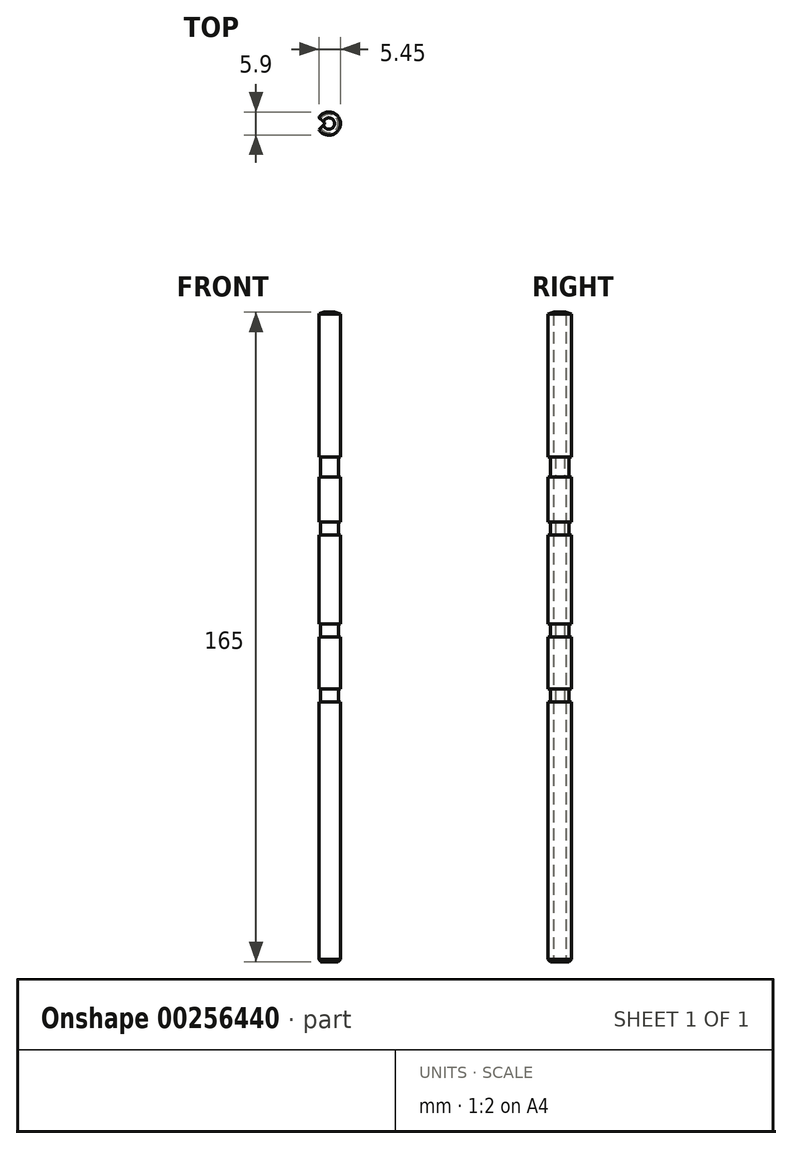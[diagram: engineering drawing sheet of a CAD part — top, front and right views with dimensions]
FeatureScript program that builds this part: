
annotation { "Feature Type Name" : "Feature", "Feature Type Description" : "" }
export const myFeature = defineFeature(function(context is Context, id is Id, definition is map)
    precondition{}
    {
        {
            var Q0;
            Q0=qCreatedBy(makeId("Top.planeOp"),FACE);
            var sketch = newSketch(context, id + "F0", { "sketchPlane" : qUnion([Q0])});
            skArc(sketch, "E0", {"start": v(-0.83, -0.52) * mm, "mid": v(0.98, 0) * mm, "end": v(-0.83, 0.52) * mm});
            skLineSegment(sketch, "E1", {"start": v(0.98, 0) * mm, "end": v(-0.32, 0) * mm, "construction": true});
            skLineSegment(sketch, "E2", {"start": v(-0.39, 0.07) * mm, "end": v(-0.83, 0.52) * mm});
            skLineSegment(sketch, "E3", {"start": v(-0.39, -0.07) * mm, "end": v(-0.83, -0.52) * mm});
            skPoint(sketch, "E4.visualSharp", {"position": v(-0.32, 0) * mm});
            skArc(sketch, "E4.filletArc", {"start": v(-0.39, -0.07) * mm, "mid": v(-0.36, 0) * mm, "end": v(-0.39, 0.07) * mm});
            skSolve(sketch);
        }
        {
            var Q0;
            Q0=makeQuery(id+"F0.imprint","IMPRINT",FACE,{"disambiguationData":[TD([[makeQuery(id+"F0.imprint","IMPRINT",EDGE,{"derivedFrom":sQuery(id+"F0.wireOp",EDGE,"E0")}),1.0]])]});
            extrude(context, id + "F1", {"entities" : qUnion([Q0]), "depth" : 55 * mm});
        }
        {
            var Q0;
            Q0=makeQuery(id+"F1.opExtrude","CAP_EDGE",EDGE,{"disambiguationData":[OSD([sQuery(id+"F0.wireOp",EDGE,"E0")])],"isStart":true});
            chamfer(context, id + "F2", {"entities" : qUnion([Q0]), "chamferType" : ChamferType.OFFSET_ANGLE, "width" : .2 * mm, "oppositeDirection" : false, "angle" : 45 * degree, "tangentPropagation" : true});
        }
        {
            var Q0;
            Q0=makeQuery(id+"F1.opExtrude","CAP_EDGE",EDGE,{"disambiguationData":[OSD([sQuery(id+"F0.wireOp",EDGE,"E0")])],"isStart":false});
            chamfer(context, id + "F3", {"entities" : qUnion([Q0]), "chamferType" : ChamferType.OFFSET_ANGLE, "width" : 0.13 * mm, "oppositeDirection" : false, "angle" : 75 * degree, "tangentPropagation" : true});
        }
        {
            var Q0;
            Q0=makeQuery(id+"F1.opExtrude","SWEPT_BODY",BODY,{"disambiguationData":[OSD([sQuery(id+"F0.wireOp",EDGE,"E0"),sQuery(id+"F0.wireOp",EDGE,"E2"),sQuery(id+"F0.wireOp",EDGE,"E3"),sQuery(id+"F0.wireOp",EDGE,"E4.filletArc")])]});
            var Q1;
            Q1=qCreatedBy(makeId("Origin.pointOp"),VERTEX);
            transform(context, id + "F4", {"entities" : qUnion([Q0]), "transformType" : TransformType.COPY});
        }
        {
            var Q0;
            Q0=makeQuery(id+"F4.opPattern","COPY",FACE,{"derivedFrom":makeQuery(id+"F1.opExtrude","CAP_FACE",FACE,{"disambiguationData":[OSD([sQuery(id+"F0.wireOp",EDGE,"E0"),sQuery(id+"F0.wireOp",EDGE,"E2"),sQuery(id+"F0.wireOp",EDGE,"E3"),sQuery(id+"F0.wireOp",EDGE,"E4.filletArc")])],"isStart":false}),"instanceName":"1"});
            cPlane(context, id + "F5", {"entities" : qUnion([Q0]), "cplaneType" : CPlaneType.OFFSET, "offset" : 18.85 * mm, "oppositeDirection" : true, "width" : 150 * mm, "height" : 150 * mm});
        }
        {
            var Q0;
            Q0=qCreatedBy(id+"F5.planeOp",FACE);
            var sketch = newSketch(context, id + "F6", { "sketchPlane" : qUnion([Q0])});
            skCircle(sketch, "E5", {"center": v(0, 0) * mm, "radius": 1.05 * mm});
            skCircle(sketch, "E6", {"center": v(0, 0) * mm, "radius": 0.8 * mm});
            skSolve(sketch);
        }
        {
            var Q0;
            Q0=makeQuery(id+"F6.imprint","IMPRINT",FACE,{"disambiguationData":[TD([[makeQuery(id+"F6.imprint","IMPRINT",EDGE,{"derivedFrom":sQuery(id+"F6.wireOp",EDGE,"E5")}),1.0]])]});
            extrude(context, id + "F7", {"entities" : qUnion([Q0]), "operationType" : NewBodyOperationType.REMOVE, "depth" : 1.1 * mm});
        }
        {
            var Q0;
            Q0=qCreatedBy(id+"F5.planeOp",FACE);
            cPlane(context, id + "F8", {"entities" : qUnion([Q0]), "cplaneType" : CPlaneType.OFFSET, "offset" : 5.5 * mm, "width" : 150 * mm, "height" : 150 * mm});
        }
        {
            var Q0;
            Q0=qCreatedBy(id+"F8.planeOp",FACE);
            var sketch = newSketch(context, id + "F9", { "sketchPlane" : qUnion([Q0])});
            skCircle(sketch, "E7", {"center": v(0, 0) * mm, "radius": 1.05 * mm});
            skCircle(sketch, "E8", {"center": v(0, 0) * mm, "radius": 0.8 * mm});
            skSolve(sketch);
        }
        {
            var Q0;
            Q0=makeQuery(id+"F9.imprint","IMPRINT",FACE,{"disambiguationData":[TD([[makeQuery(id+"F9.imprint","IMPRINT",EDGE,{"derivedFrom":sQuery(id+"F9.wireOp",EDGE,"E7")}),1.0]])]});
            extrude(context, id + "F10", {"entities" : qUnion([Q0]), "operationType" : NewBodyOperationType.REMOVE, "depth" : 1.1 * mm});
        }
        {
            var Q0;
            Q0=makeQuery(id+"F1.opExtrude","SWEPT_BODY",BODY,{"disambiguationData":[OSD([sQuery(id+"F0.wireOp",EDGE,"E0"),sQuery(id+"F0.wireOp",EDGE,"E2"),sQuery(id+"F0.wireOp",EDGE,"E3"),sQuery(id+"F0.wireOp",EDGE,"E4.filletArc")])]});
            transform(context, id + "F11", {"entities" : qUnion([Q0]), "transformType" : TransformType.TRANSLATION_3D, "dx" : 0 * mm, "dy" : 0 * mm, "dz" : 0 * mm, "makeCopy" : true});
        }
        {
            var Q0;
            Q0=makeQuery(id+"F11.opPattern","COPY",FACE,{"derivedFrom":makeQuery(id+"F1.opExtrude","CAP_FACE",FACE,{"disambiguationData":[OSD([sQuery(id+"F0.wireOp",EDGE,"E0"),sQuery(id+"F0.wireOp",EDGE,"E2"),sQuery(id+"F0.wireOp",EDGE,"E3"),sQuery(id+"F0.wireOp",EDGE,"E4.filletArc")])],"isStart":false}),"instanceName":"1"});
            cPlane(context, id + "F12", {"entities" : qUnion([Q0]), "cplaneType" : CPlaneType.OFFSET, "offset" : 33 * mm, "oppositeDirection" : true, "width" : 150 * mm, "height" : 150 * mm});
        }
        {
            var Q0;
            Q0=qCreatedBy(id+"F12.planeOp",FACE);
            var sketch = newSketch(context, id + "F13", { "sketchPlane" : qUnion([Q0])});
            skCircle(sketch, "E9", {"center": v(0, 0) * mm, "radius": 1.05 * mm});
            skCircle(sketch, "E10", {"center": v(0, 0) * mm, "radius": 0.8 * mm});
            skSolve(sketch);
        }
        {
            var Q0;
            Q0=makeQuery(id+"F13.imprint","IMPRINT",FACE,{"disambiguationData":[TD([[makeQuery(id+"F13.imprint","IMPRINT",EDGE,{"derivedFrom":sQuery(id+"F13.wireOp",EDGE,"E9")}),1.0]])]});
            extrude(context, id + "F14", {"entities" : qUnion([Q0]), "operationType" : NewBodyOperationType.REMOVE, "depth" : 1.1 * mm});
        }
        {
            var Q0;
            Q0=qCreatedBy(id+"F12.planeOp",FACE);
            cPlane(context, id + "F15", {"entities" : qUnion([Q0]), "cplaneType" : CPlaneType.OFFSET, "offset" : 5.5 * mm, "width" : 150 * mm, "height" : 150 * mm});
        }
        {
            var Q0;
            Q0=qCreatedBy(id+"F15.planeOp",FACE);
            var sketch = newSketch(context, id + "F16", { "sketchPlane" : qUnion([Q0])});
            skCircle(sketch, "E11", {"center": v(0, 0) * mm, "radius": 1.05 * mm});
            skCircle(sketch, "E12", {"center": v(0, 0) * mm, "radius": 0.8 * mm});
            skSolve(sketch);
        }
        {
            var Q0;
            Q0=makeQuery(id+"F16.imprint","IMPRINT",FACE,{"disambiguationData":[TD([[makeQuery(id+"F16.imprint","IMPRINT",EDGE,{"derivedFrom":sQuery(id+"F16.wireOp",EDGE,"E11")}),1.0]])]});
            extrude(context, id + "F17", {"entities" : qUnion([Q0]), "operationType" : NewBodyOperationType.REMOVE, "depth" : 1.1 * mm});
        }
        {
            var Q0;
            Q0=makeQuery(id+"F11.opPattern","COPY",FACE,{"derivedFrom":makeQuery(id+"F1.opExtrude","CAP_FACE",FACE,{"disambiguationData":[OSD([sQuery(id+"F0.wireOp",EDGE,"E0"),sQuery(id+"F0.wireOp",EDGE,"E2"),sQuery(id+"F0.wireOp",EDGE,"E3"),sQuery(id+"F0.wireOp",EDGE,"E4.filletArc")])],"isStart":false}),"instanceName":"1"});
            cPlane(context, id + "F18", {"entities" : qUnion([Q0]), "cplaneType" : CPlaneType.OFFSET, "offset" : 13.95 * mm, "oppositeDirection" : true, "width" : 150 * mm, "height" : 150 * mm});
        }
        {
            var Q0;
            Q0=qCreatedBy(id+"F18.planeOp",FACE);
            var sketch = newSketch(context, id + "F19", { "sketchPlane" : qUnion([Q0])});
            skCircle(sketch, "E13", {"center": v(0, 0) * mm, "radius": 0.98 * mm});
            skCircle(sketch, "E14", {"center": v(0, 0) * mm, "radius": 0.8 * mm});
            skSolve(sketch);
        }
        {
            var Q0;
            Q0=makeQuery(id+"F1.opExtrude","SWEPT_BODY",BODY,{"disambiguationData":[OSD([sQuery(id+"F0.wireOp",EDGE,"E0"),sQuery(id+"F0.wireOp",EDGE,"E2"),sQuery(id+"F0.wireOp",EDGE,"E3"),sQuery(id+"F0.wireOp",EDGE,"E4.filletArc")])]});
            transform(context, id + "F20", {"entities" : qUnion([Q0]), "transformType" : TransformType.TRANSLATION_3D, "dx" : 0 * mm, "dy" : 0 * mm, "dz" : 0 * mm, "makeCopy" : true});
        }
        {
            var Q0;
            Q0=makeQuery(id+"F19.imprint","IMPRINT",FACE,{"disambiguationData":[TD([[makeQuery(id+"F19.imprint","IMPRINT",EDGE,{"derivedFrom":sQuery(id+"F19.wireOp",EDGE,"E13")}),1.0]])]});
            extrude(context, id + "F21", {"entities" : qUnion([Q0]), "operationType" : NewBodyOperationType.REMOVE, "depth" : 1.1 * mm});
        }
        {
            var Q0;
            Q0=makeQuery(id+"F1.opExtrude","SWEPT_BODY",BODY,{"disambiguationData":[OSD([sQuery(id+"F0.wireOp",EDGE,"E0"),sQuery(id+"F0.wireOp",EDGE,"E2"),sQuery(id+"F0.wireOp",EDGE,"E3"),sQuery(id+"F0.wireOp",EDGE,"E4.filletArc")])]});
            var Q1;
            Q1=makeQuery(id+"F4.opPattern","COPY",BODY,{"derivedFrom":makeQuery(id+"F1.opExtrude","SWEPT_BODY",BODY,{"disambiguationData":[OSD([sQuery(id+"F0.wireOp",EDGE,"E0"),sQuery(id+"F0.wireOp",EDGE,"E2"),sQuery(id+"F0.wireOp",EDGE,"E3"),sQuery(id+"F0.wireOp",EDGE,"E4.filletArc")])]}),"instanceName":"1"});
            var Q2;
            Q2=makeQuery(id+"F11.opPattern","COPY",BODY,{"derivedFrom":makeQuery(id+"F1.opExtrude","SWEPT_BODY",BODY,{"disambiguationData":[OSD([sQuery(id+"F0.wireOp",EDGE,"E0"),sQuery(id+"F0.wireOp",EDGE,"E2"),sQuery(id+"F0.wireOp",EDGE,"E3"),sQuery(id+"F0.wireOp",EDGE,"E4.filletArc")])]}),"instanceName":"1"});
            var Q3;
            Q3=makeQuery(id+"F20.opPattern","COPY",BODY,{"derivedFrom":makeQuery(id+"F1.opExtrude","SWEPT_BODY",BODY,{"disambiguationData":[OSD([sQuery(id+"F0.wireOp",EDGE,"E0"),sQuery(id+"F0.wireOp",EDGE,"E2"),sQuery(id+"F0.wireOp",EDGE,"E3"),sQuery(id+"F0.wireOp",EDGE,"E4.filletArc")])]}),"instanceName":"1"});
            var Q4;
            Q4=qCreatedBy(makeId("Origin.pointOp"),VERTEX);
            transform(context, id + "F22", {"entities" : qUnion([Q0, Q1, Q2, Q3]), "transformType" : TransformType.SCALE_UNIFORMLY, "scale" : 3, "makeCopy" : false, "scalePoint" : qUnion([Q4])});
        }
    });
